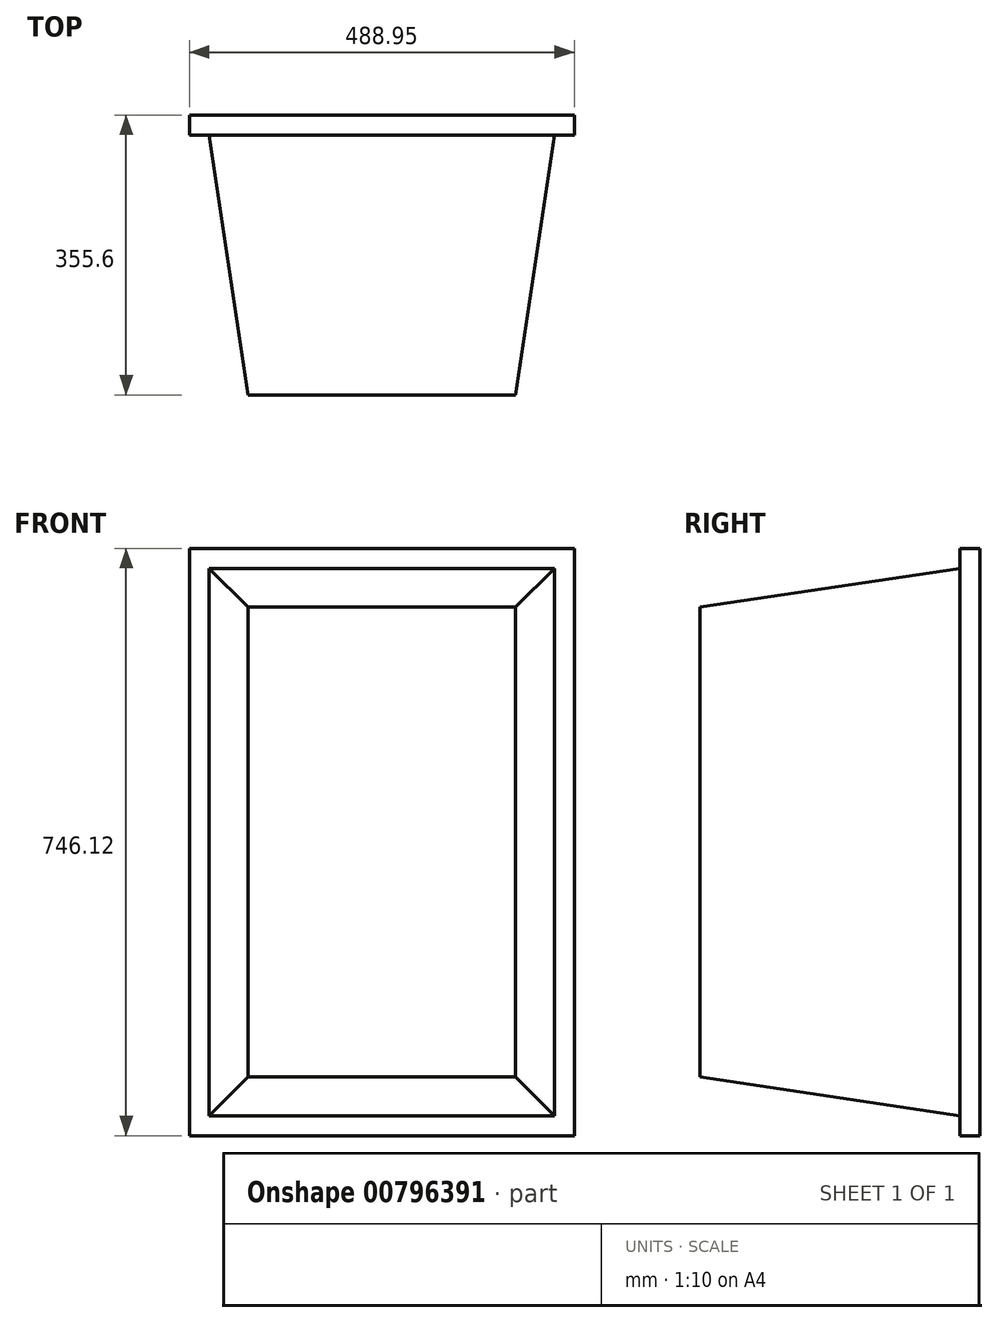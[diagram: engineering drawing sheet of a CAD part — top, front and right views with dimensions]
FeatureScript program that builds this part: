
annotation { "Feature Type Name" : "Feature", "Feature Type Description" : "" }
export const myFeature = defineFeature(function(context is Context, id is Id, definition is map)
    precondition{}
    {
        {
            var Q0;
            Q0=qCreatedBy(makeId("Top.planeOp"),FACE);
            var sketch = newSketch(context, id + "F0", { "sketchPlane" : qUnion([Q0])});
            skLineSegment(sketch, "E0.bottom", {"start": v(-71.37, 60.91) * mm, "end": v(366.78, 60.91) * mm});
            skLineSegment(sketch, "E0.top", {"start": v(-22.16, -269.29) * mm, "end": v(317.57, -269.29) * mm});
            skLineSegment(sketch, "E0.left", {"start": v(-71.37, 60.91) * mm, "end": v(-22.16, -269.29) * mm});
            skLineSegment(sketch, "E0.right", {"start": v(366.78, 60.91) * mm, "end": v(317.57, -269.29) * mm});
            skLineSegment(sketch, "E1.bottom", {"start": v(-96.77, 86.31) * mm, "end": v(392.18, 86.31) * mm});
            skLineSegment(sketch, "E1.top", {"start": v(-96.77, 60.91) * mm, "end": v(392.18, 60.91) * mm});
            skLineSegment(sketch, "E1.left", {"start": v(-96.77, 86.31) * mm, "end": v(-96.77, 60.91) * mm});
            skLineSegment(sketch, "E1.right", {"start": v(392.18, 86.31) * mm, "end": v(392.18, 60.91) * mm});
            skSolve(sketch);
        }
        {
            var Q0;
            {var subQ2=sQuery(id+"F0.wireOp",EDGE,"E0.bottom");var subQ6=makeQuery(id+"F0.imprint","IMPRINT",EDGE,{"derivedFrom":subQ2});Q0=qUnion([makeQuery(id+"F0.imprint","IMPRINT",FACE,{"disambiguationData":[TD([[subQ6,-1.0]])]}),makeQuery(id+"F0.imprint","IMPRINT",FACE,{"disambiguationData":[TD([[subQ6,1.0]])]})]);}
            extrude(context, id + "F1", {"entities" : qUnion([Q0]), "depth" : 746.12 * mm, "offsetDistance" : 25.4 * mm});
        }
        {
            var Q0;
            Q0=makeQuery(id+"F1.opExtrude","SWEPT_FACE",FACE,{"disambiguationData":[OSD([sQuery(id+"F0.wireOp",EDGE,"E1.right")])]});
            var sketch = newSketch(context, id + "F2", { "sketchPlane" : qUnion([Q0])});
            skLineSegment(sketch, "E2", {"start": v(60.91, 746.12) * mm, "end": v(60.91, 720.73) * mm});
            skLineSegment(sketch, "E3", {"start": v(60.91, 720.73) * mm, "end": v(-269.29, 671.5) * mm});
            skLineSegment(sketch, "E4", {"start": v(-269.29, 671.5) * mm, "end": v(-269.29, 746.12) * mm});
            skLineSegment(sketch, "E5", {"start": v(-269.29, 746.12) * mm, "end": v(60.91, 746.12) * mm});
            skLineSegment(sketch, "E6", {"start": v(-269.29, 0) * mm, "end": v(-269.29, 74.63) * mm});
            skLineSegment(sketch, "E7", {"start": v(-269.29, 74.63) * mm, "end": v(60.91, 25.4) * mm});
            skLineSegment(sketch, "E8", {"start": v(60.91, 25.4) * mm, "end": v(60.91, 0) * mm});
            skLineSegment(sketch, "E9", {"start": v(60.91, 0) * mm, "end": v(-269.29, 0) * mm});
            skSolve(sketch);
        }
        {
            var Q0;
            Q0 = qSketchRegion(id + "F2", true);
            extrude(context, id + "F3", {"entities" : qUnion([Q0]), "operationType" : NewBodyOperationType.REMOVE, "endBound" : BoundingType.THROUGH_ALL, "oppositeDirection" : true, "depth" : 25.4 * mm, "offsetDistance" : 25.4 * mm});
        }
    });
